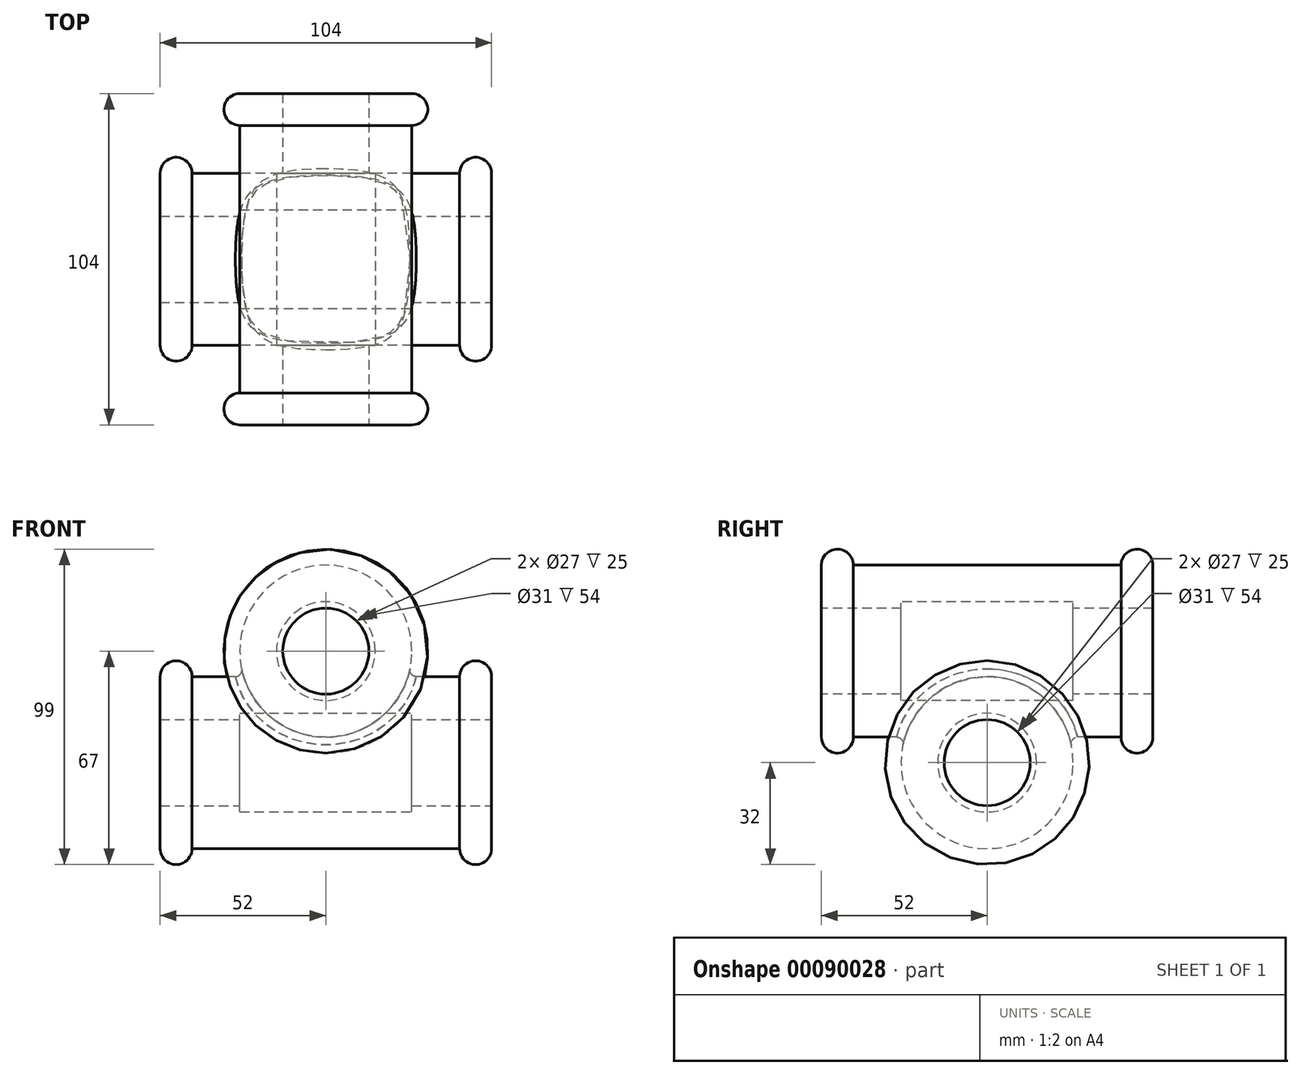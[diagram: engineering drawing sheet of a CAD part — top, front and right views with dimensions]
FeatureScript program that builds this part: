
annotation { "Feature Type Name" : "Feature", "Feature Type Description" : "" }
export const myFeature = defineFeature(function(context is Context, id is Id, definition is map)
    precondition{}
    {
        {
            var Q0;
            Q0=qCreatedBy(makeId("Front.planeOp"),FACE);
            var sketch = newSketch(context, id + "F0", { "sketchPlane" : qUnion([Q0])});
            skLineSegment(sketch, "E0", {"start": v(-52, 0) * mm, "end": v(52, 0) * mm});
            skLineSegment(sketch, "E1", {"start": v(0, 27) * mm, "end": v(0, 0) * mm, "construction": true});
            skLineSegment(sketch, "E2", {"start": v(-52, 0) * mm, "end": v(-52, 27) * mm});
            skArc(sketch, "E3", {"start": v(-42, 27) * mm, "mid": v(-47, 32) * mm, "end": v(-52, 27) * mm});
            skLineSegment(sketch, "E4.trimOffspring", {"start": v(-42, 27) * mm, "end": v(0, 27) * mm});
            skLineSegment(sketch, "E5.MirrorCS", {"start": v(42, 27) * mm, "end": v(0, 27) * mm});
            skArc(sketch, "E6.MirrorCS", {"start": v(42, 27) * mm, "mid": v(47, 32) * mm, "end": v(52, 27) * mm});
            skLineSegment(sketch, "E7.MirrorCS", {"start": v(52, 0) * mm, "end": v(52, 27) * mm});
            skSolve(sketch);
        }
        {
            var Q0;
            Q0=makeQuery(id+"F0.imprint","IMPRINT",FACE,{"disambiguationData":[TD([[makeQuery(id+"F0.imprint","IMPRINT",EDGE,{"derivedFrom":sQuery(id+"F0.wireOp",EDGE,"E0")}),1.0]])]});
            var Q1;
            Q1=sQuery(id+"F0.wireOp",EDGE,"E0");
            revolve(context, id + "F1", {"entities" : qUnion([Q0]), "axis" : qUnion([Q1]), "revolveType" : RevolveType.FULL});
        }
        {
            var Q0;
            Q0=qCreatedBy(makeId("Right.planeOp"),FACE);
            var sketch = newSketch(context, id + "F2", { "sketchPlane" : qUnion([Q0])});
            skLineSegment(sketch, "E8", {"start": v(-52, 35) * mm, "end": v(52, 35) * mm});
            skLineSegment(sketch, "E9", {"start": v(-52, 35) * mm, "end": v(-52, 62) * mm});
            skLineSegment(sketch, "E10", {"start": v(52, 35) * mm, "end": v(52, 62) * mm});
            skArc(sketch, "E11", {"start": v(-42, 62) * mm, "mid": v(-47, 67) * mm, "end": v(-52, 62) * mm});
            skArc(sketch, "E12", {"start": v(52, 62) * mm, "mid": v(47, 67) * mm, "end": v(42, 62) * mm});
            skLineSegment(sketch, "E13.trimOffspring", {"start": v(-42, 62) * mm, "end": v(42, 62) * mm});
            skSolve(sketch);
        }
        {
            var Q0;
            Q0=makeQuery(id+"F2.imprint","IMPRINT",FACE,{"disambiguationData":[TD([[makeQuery(id+"F2.imprint","IMPRINT",EDGE,{"derivedFrom":sQuery(id+"F2.wireOp",EDGE,"E8")}),1.0]])]});
            var Q1;
            Q1=sQuery(id+"F2.wireOp",EDGE,"E8");
            revolve(context, id + "F3", {"operationType" : NewBodyOperationType.ADD, "entities" : qUnion([Q0]), "axis" : qUnion([Q1]), "revolveType" : RevolveType.FULL});
        }
        {
            var Q0;
            Q0=qCreatedBy(makeId("Front.planeOp"),FACE);
            var sketch = newSketch(context, id + "F4", { "sketchPlane" : qUnion([Q0])});
            skCircle(sketch, "E14", {"center": v(0, 35) * mm, "radius": 15.5 * mm});
            skCircle(sketch, "E15", {"center": v(0, 35) * mm, "radius": 13.5 * mm});
            skSolve(sketch);
        }
        {
            var Q0;
            Q0=makeQuery(id+"F4.imprint","IMPRINT",FACE,{"disambiguationData":[TD([[makeQuery(id+"F4.imprint","IMPRINT",EDGE,{"derivedFrom":sQuery(id+"F4.wireOp",EDGE,"E15")}),1.0]])]});
            extrude(context, id + "F5", {"entities" : qUnion([Q0]), "operationType" : NewBodyOperationType.REMOVE, "oppositeDirection" : true, "depth" : 104 * mm, "symmetric" : true});
        }
        {
            var Q0;
            Q0=makeQuery(id+"F4.imprint","IMPRINT",FACE,{"disambiguationData":[TD([[makeQuery(id+"F4.imprint","IMPRINT",EDGE,{"derivedFrom":sQuery(id+"F4.wireOp",EDGE,"E14")}),1.0]])]});
            extrude(context, id + "F6", {"entities" : qUnion([Q0]), "operationType" : NewBodyOperationType.REMOVE, "oppositeDirection" : true, "depth" : 54 * mm, "symmetric" : true});
        }
        {
            var Q0;
            Q0=qCreatedBy(makeId("Right.planeOp"),FACE);
            var sketch = newSketch(context, id + "F7", { "sketchPlane" : qUnion([Q0])});
            skCircle(sketch, "E16", {"center": v(0, 0) * mm, "radius": 15.5 * mm});
            skCircle(sketch, "E17", {"center": v(0, 0) * mm, "radius": 13.5 * mm});
            skSolve(sketch);
        }
        {
            var Q0;
            Q0=makeQuery(id+"F7.imprint","IMPRINT",FACE,{"disambiguationData":[TD([[makeQuery(id+"F7.imprint","IMPRINT",EDGE,{"derivedFrom":sQuery(id+"F7.wireOp",EDGE,"E17")}),1.0]])]});
            extrude(context, id + "F8", {"entities" : qUnion([Q0]), "operationType" : NewBodyOperationType.REMOVE, "oppositeDirection" : true, "depth" : 104 * mm, "symmetric" : true});
        }
        {
            var Q0;
            Q0=makeQuery(id+"F7.imprint","IMPRINT",FACE,{"disambiguationData":[TD([[makeQuery(id+"F7.imprint","IMPRINT",EDGE,{"derivedFrom":sQuery(id+"F7.wireOp",EDGE,"E16")}),1.0]])]});
            extrude(context, id + "F9", {"entities" : qUnion([Q0]), "operationType" : NewBodyOperationType.REMOVE, "oppositeDirection" : true, "depth" : 54 * mm, "symmetric" : true});
        }
        {
            var Q0;
            Q0=makeQuery(id+"F3.boolean.opBoolean","INTERSECT",EDGE,{"derivedFrom":[makeQuery(id+"F1.opRevolve","SWEPT_FACE",FACE,{"disambiguationData":[OSD([sQuery(id+"F0.wireOp",EDGE,"E4.trimOffspring"),sQuery(id+"F0.wireOp",EDGE,"E5.MirrorCS")])]}),makeQuery(id+"F3.opRevolve","SWEPT_FACE",FACE,{"disambiguationData":[OSD([sQuery(id+"F2.wireOp",EDGE,"E13.trimOffspring")])]})]});
            fillet(context, id + "F10", {"entities" : qUnion([Q0]), "radius" : 2 * mm, "tangentPropagation" : true, "allowEdgeOverflow" : false});
        }
    });
